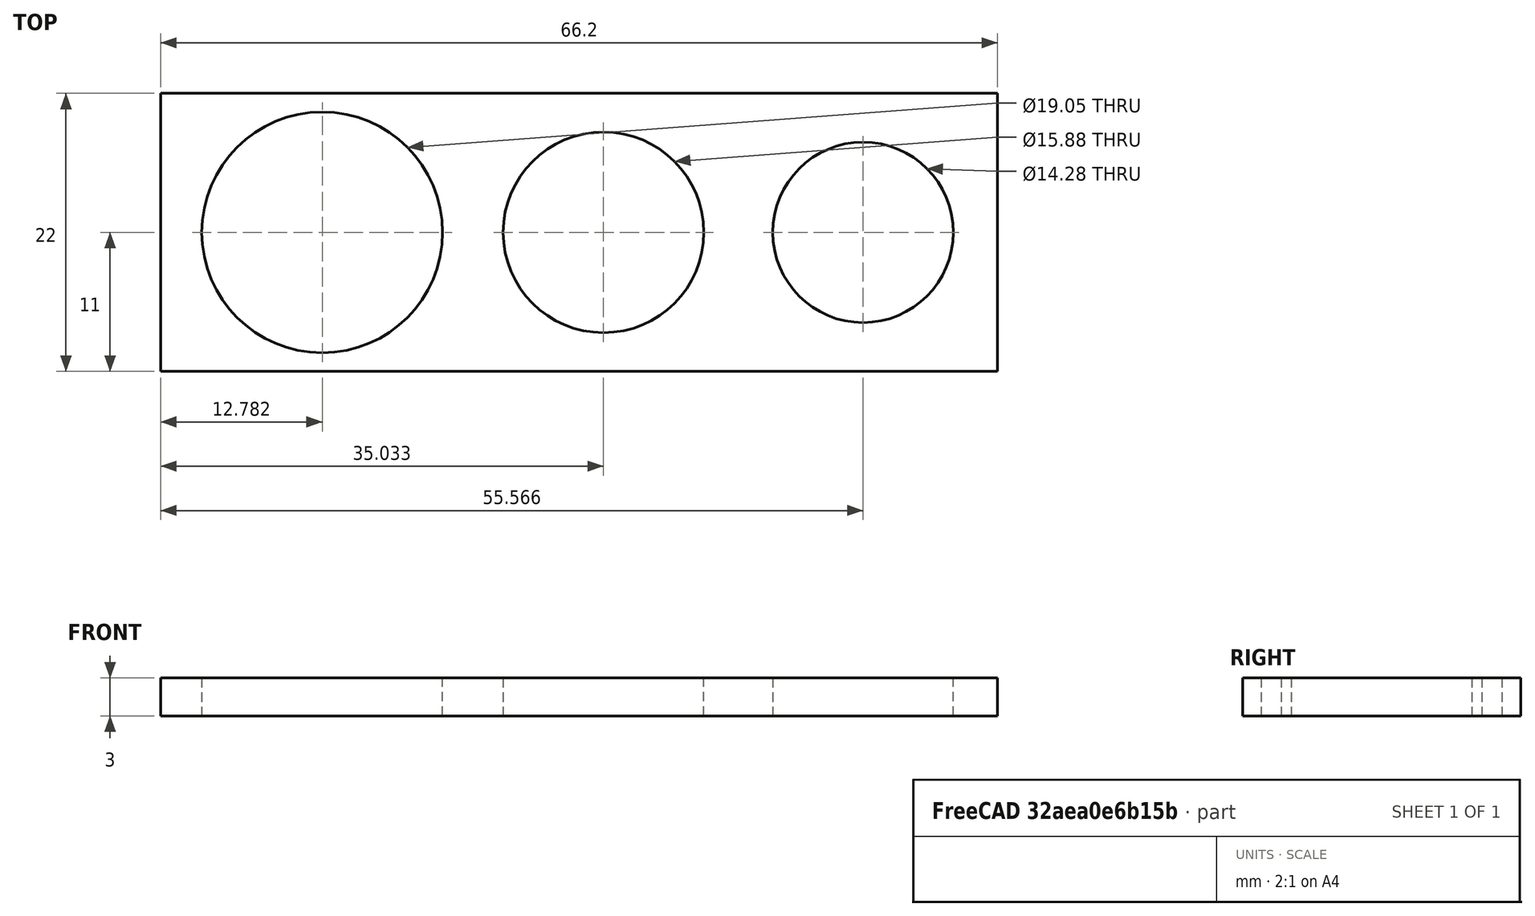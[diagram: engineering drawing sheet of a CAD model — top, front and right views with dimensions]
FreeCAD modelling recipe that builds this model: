
FCSTD DOCUMENT  (FreeCAD 0.19R)
Label: BoltGage
License: All rights reserved
LicenseURL: http://en.wikipedia.org/wiki/All_rights_reserved
objects: Sketcher::SketchObject×1, PartDesign::Pad×1, PartDesign::Body×1, Mesh::Feature×1
note: 4 computed .brp shape members not serialized (recipe doc carries the construction recipe); baked Part::Feature solids carry a one-line shape summary decoded from their .brp

FEATURE [Sketcher::SketchObject] Sketch
  FullyConstrained = false
  MapMode = 5
  Support = -> [XY_Plane]
  sketch-geometry (7):
    g0: LineSegment StartX=-33.1046 StartY=11 StartZ=0 EndX=33.1046 EndY=11 EndZ=0
    g1: LineSegment StartX=33.1046 StartY=11 StartZ=0 EndX=33.1046 EndY=-11 EndZ=0
    g2: LineSegment StartX=33.1046 StartY=-11 StartZ=0 EndX=-33.1046 EndY=-11 EndZ=0
    g3: LineSegment StartX=-33.1046 StartY=-11 StartZ=0 EndX=-33.1046 EndY=11 EndZ=0
    g4: Circle CenterX=-20.3179 CenterY=0 CenterZ=0 NormalX=0 NormalY=0 NormalZ=1 AngleXU=0 Radius=9.525
    g5: Circle CenterX=1.93299 CenterY=0 CenterZ=0 NormalX=0 NormalY=0 NormalZ=1 AngleXU=0 Radius=7.9375
    g6: Circle CenterX=22.4656 CenterY=0 CenterZ=0 NormalX=0 NormalY=0 NormalZ=1 AngleXU=0 Radius=7.14
  constraints (16):
    c: Coincident(g0,g1)
    c: Coincident(g1,g2)
    c: Coincident(g2,g3)
    c: Coincident(g3,g0)
    c: Horizontal(g0)
    c: Horizontal(g2)
    c: Vertical(g1)
    c: Vertical(g3)
    c: Symmetric(g1,g0,g-1)
    c: Distance(g3) = 22
    c: PointOnObject(g4,g-1)
    c: PointOnObject(g5,g-1)
    c: PointOnObject(g6,g-1)
    c: Diameter(g4) = 19.05
    c: Diameter(g5) = 15.875
    c: Diameter(g6) = 14.28
FEATURE [PartDesign::Pad] Pad
  Direction = (1,1,1)
  Length = 3
  Length2 = 100
  Profile = -> Sketch
  Type = 0
FEATURE [PartDesign::Body] Body
  Group = -> [Sketch,Pad]
  Origin = -> Origin
  Tip = -> Pad
FEATURE [Mesh::Feature] Mesh  label="Pad (Meshed)"
